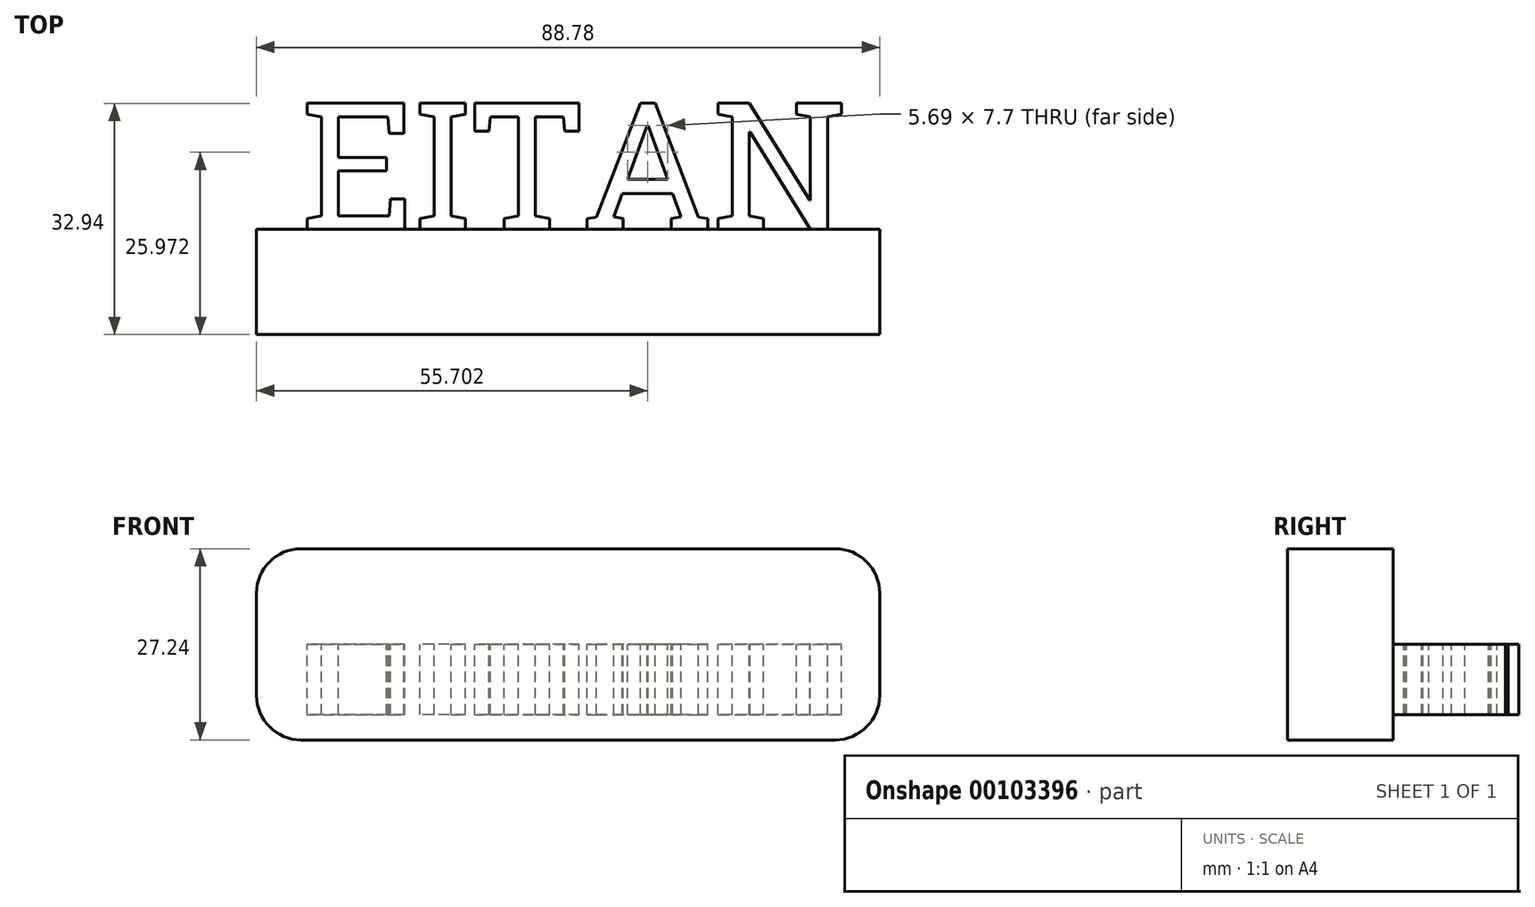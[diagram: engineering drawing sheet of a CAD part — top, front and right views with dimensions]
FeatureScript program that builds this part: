
annotation { "Feature Type Name" : "Feature", "Feature Type Description" : "" }
export const myFeature = defineFeature(function(context is Context, id is Id, definition is map)
    precondition{}
    {
        {
            var Q0;
            Q0=qCreatedBy(makeId("Front.planeOp"),FACE);
            var sketch = newSketch(context, id + "F0", { "sketchPlane" : qUnion([Q0])});
            skLineSegment(sketch, "E0.bottom", {"start": v(-38.04, -13.62) * mm, "end": v(38.04, -13.62) * mm});
            skLineSegment(sketch, "E0.top", {"start": v(-38.04, 13.62) * mm, "end": v(38.04, 13.62) * mm});
            skLineSegment(sketch, "E0.left", {"start": v(-44.4, -7.27) * mm, "end": v(-44.4, 7.27) * mm});
            skLineSegment(sketch, "E0.right", {"start": v(44.4, -7.27) * mm, "end": v(44.4, 7.27) * mm});
            skPoint(sketch, "E0.middle", {"position": v(0, 0) * mm});
            skPoint(sketch, "E1.visualSharp", {"position": v(-44.4, 13.62) * mm});
            skArc(sketch, "E1.filletArc", {"start": v(-38.04, 13.62) * mm, "mid": v(-42.53, 11.76) * mm, "end": v(-44.4, 7.27) * mm});
            skPoint(sketch, "E2.visualSharp", {"position": v(44.4, 13.62) * mm});
            skArc(sketch, "E2.filletArc", {"start": v(44.4, 7.27) * mm, "mid": v(42.53, 11.76) * mm, "end": v(38.04, 13.62) * mm});
            skPoint(sketch, "E3.visualSharp", {"position": v(44.4, -13.62) * mm});
            skArc(sketch, "E3.filletArc", {"start": v(38.04, -13.62) * mm, "mid": v(42.53, -11.76) * mm, "end": v(44.4, -7.27) * mm});
            skPoint(sketch, "E4.visualSharp", {"position": v(-44.4, -13.62) * mm});
            skArc(sketch, "E4.filletArc", {"start": v(-44.4, -7.27) * mm, "mid": v(-42.53, -11.76) * mm, "end": v(-38.04, -13.62) * mm});
            skSolve(sketch);
        }
        {
            var Q0;
            Q0=qCreatedBy(makeId("Top.planeOp"),FACE);
            var sketch = newSketch(context, id + "F1", { "sketchPlane" : qUnion([Q0])});
            skText(sketch, "E5", { "text": "EITAN", "fontName": "RobotoSlab-Regular.ttf"});
            const initialGuessF1  = {"E5": [-0.03804, 0, 1, 0, 0.01817]};
            skSetInitialGuess(sketch, initialGuessF1);
            skSolve(sketch);
        }
        {
            var Q0;
            Q0=makeQuery(id+"F0.imprint","IMPRINT",FACE,{"disambiguationData":[TD([[makeQuery(id+"F0.imprint","IMPRINT",EDGE,{"derivedFrom":sQuery(id+"F0.wireOp",EDGE,"E0.bottom")}),1.0]])]});
            extrude(context, id + "F2", {"entities" : qUnion([Q0]), "depth" : 15 * mm});
        }
        {
            var Q0;
            Q0=makeQuery(id+"F1.imprint","IMPRINT",FACE,{"disambiguationData":[TD([[makeQuery(id+"F1.imprint","IMPRINT",EDGE,{"derivedFrom":sQuery(id+"F1.wireOp",EDGE,"E5.sketch_text.stroke-0")}),-1.0]])]});
            var Q1;
            Q1=makeQuery(id+"F1.imprint","IMPRINT",FACE,{"disambiguationData":[TD([[makeQuery(id+"F1.imprint","IMPRINT",EDGE,{"derivedFrom":sQuery(id+"F1.wireOp",EDGE,"E5.sketch_text.stroke-68")}),-1.0]])]});
            var Q2;
            Q2=makeQuery(id+"F1.imprint","IMPRINT",FACE,{"disambiguationData":[TD([[makeQuery(id+"F1.imprint","IMPRINT",EDGE,{"derivedFrom":sQuery(id+"F1.wireOp",EDGE,"E5.sketch_text.stroke-32")}),-1.0]])]});
            var Q3;
            Q3=makeQuery(id+"F1.imprint","IMPRINT",FACE,{"disambiguationData":[TD([[makeQuery(id+"F1.imprint","IMPRINT",EDGE,{"derivedFrom":sQuery(id+"F1.wireOp",EDGE,"E5.sketch_text.stroke-20")}),-1.0]])]});
            var Q4;
            Q4=makeQuery(id+"F1.imprint","IMPRINT",FACE,{"disambiguationData":[TD([[makeQuery(id+"F1.imprint","IMPRINT",EDGE,{"derivedFrom":sQuery(id+"F1.wireOp",EDGE,"E5.sketch_text.stroke-48")}),-1.0]])]});
            extrude(context, id + "F3", {"entities" : qUnion([Q0, Q1, Q2, Q3, Q4]), "operationType" : NewBodyOperationType.ADD, "oppositeDirection" : true, "depth" : 10 * mm});
        }
    });
